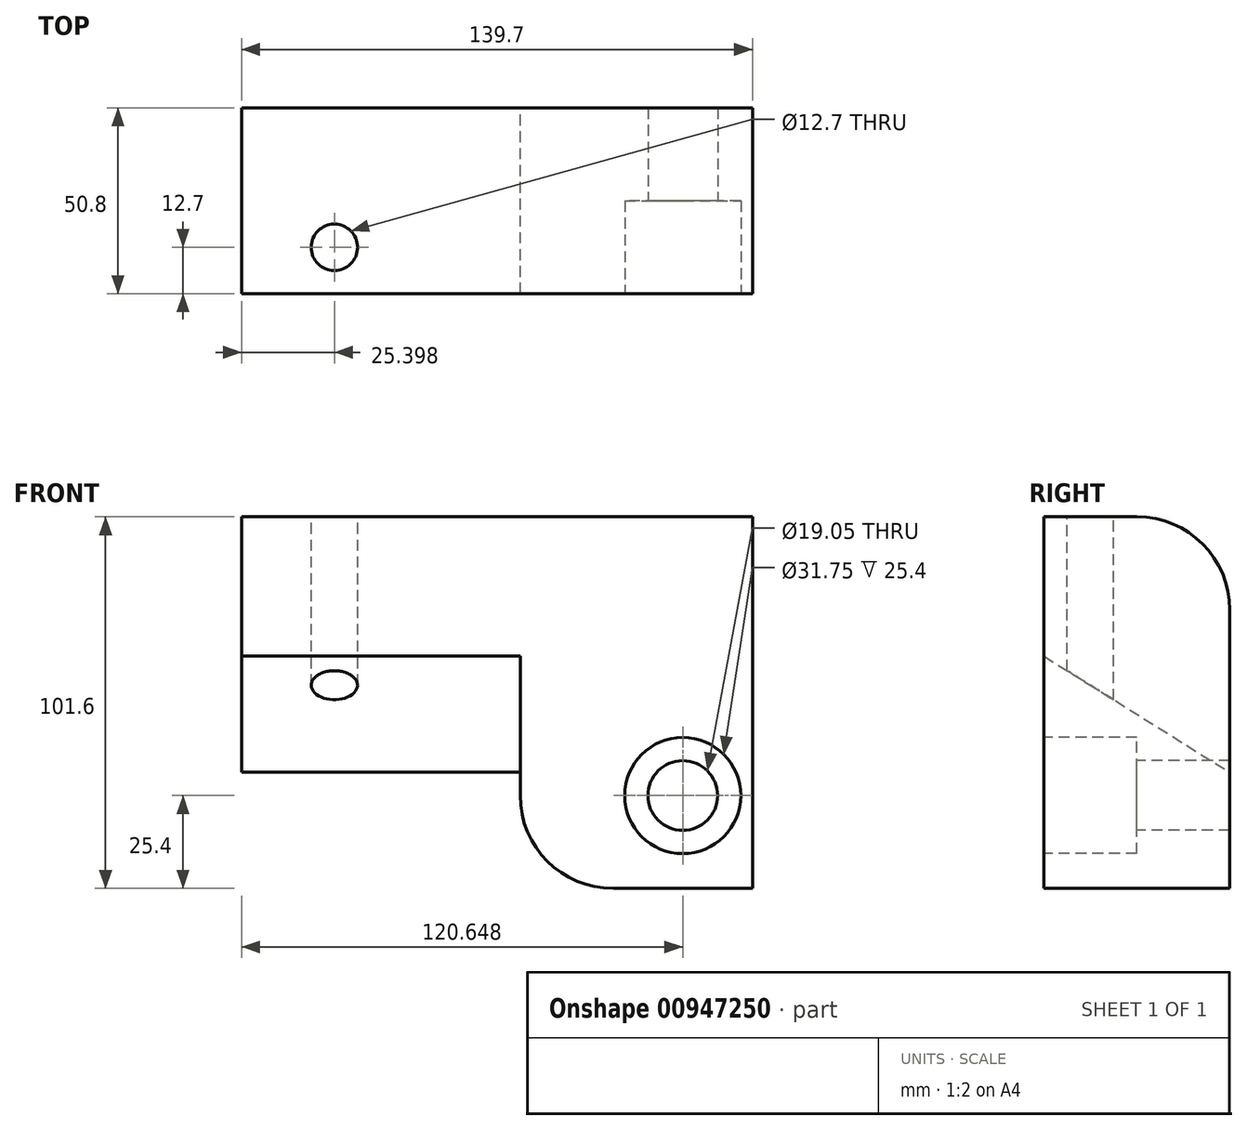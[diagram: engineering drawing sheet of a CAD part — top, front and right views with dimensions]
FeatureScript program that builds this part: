
annotation { "Feature Type Name" : "Feature", "Feature Type Description" : "" }
export const myFeature = defineFeature(function(context is Context, id is Id, definition is map)
    precondition{}
    {
        {
            var Q0;
            Q0=qCreatedBy(makeId("Front.planeOp"),FACE);
            var sketch = newSketch(context, id + "F0", { "sketchPlane" : qUnion([Q0])});
            skLineSegment(sketch, "E0.bottom", {"start": v(2.18, 50.8) * mm, "end": v(65.68, 50.8) * mm});
            skLineSegment(sketch, "E0.top", {"start": v(2.18, -50.8) * mm, "end": v(65.68, -50.8) * mm});
            skLineSegment(sketch, "E0.left", {"start": v(2.18, 50.8) * mm, "end": v(2.18, -50.8) * mm});
            skLineSegment(sketch, "E0.right", {"start": v(65.68, 50.8) * mm, "end": v(65.68, -50.8) * mm});
            skPoint(sketch, "E0.middle", {"position": v(33.93, 0) * mm});
            skLineSegment(sketch, "E1.bottom", {"start": v(2.18, 50.8) * mm, "end": v(-74.02, 50.8) * mm});
            skLineSegment(sketch, "E1.top", {"start": v(2.18, -19.05) * mm, "end": v(-74.02, -19.05) * mm});
            skLineSegment(sketch, "E1.left", {"start": v(2.18, 50.8) * mm, "end": v(2.18, -19.05) * mm});
            skLineSegment(sketch, "E1.right", {"start": v(-74.02, 50.8) * mm, "end": v(-74.02, -19.05) * mm});
            skCircle(sketch, "E2", {"center": v(46.63, -25.4) * mm, "radius": 15.88 * mm});
            skSolve(sketch);
        }
        {
            var Q0;
            Q0=makeQuery(id+"F0.imprint","IMPRINT",FACE,{"disambiguationData":[TD([[makeQuery(id+"F0.imprint","IMPRINT",EDGE,{"derivedFrom":sQuery(id+"F0.wireOp",EDGE,"E0.bottom")}),-1.0]])]});
            var Q1;
            Q1=makeQuery(id+"F0.imprint","IMPRINT",FACE,{"disambiguationData":[TD([[makeQuery(id+"F0.imprint","IMPRINT",EDGE,{"derivedFrom":sQuery(id+"F0.wireOp",EDGE,"E2")}),1.0]])]});
            var Q2;
            Q2=makeQuery(id+"F0.imprint","IMPRINT",FACE,{"disambiguationData":[TD([[makeQuery(id+"F0.imprint","IMPRINT",EDGE,{"derivedFrom":sQuery(id+"F0.wireOp",EDGE,"E1.bottom")}),1.0]])]});
            extrude(context, id + "F1", {"entities" : qUnion([Q0, Q1, Q2]), "depth" : 50.8 * mm, "offsetDistance" : 25.4 * mm});
        }
        {
            var Q0;
            Q0=makeQuery(id+"F1.opExtrude","SWEPT_EDGE",EDGE,{"disambiguationData":[OSD([sQuery(id+"F0.wireOp",EDGE,"E0.top"),sQuery(id+"F0.wireOp",EDGE,"E0.left")])]});
            fillet(context, id + "F2", {"entities" : qUnion([Q0]), "radius" : 25.4 * mm, "tangentPropagation" : true, "allowEdgeOverflow" : false});
        }
        {
            var Q0;
            Q0=makeQuery(id+"F1.opExtrude","CAP_EDGE",EDGE,{"disambiguationData":[OSD([sQuery(id+"F0.wireOp",EDGE,"E0.bottom"),sQuery(id+"F0.wireOp",EDGE,"E1.bottom")])],"isStart":true});
            fillet(context, id + "F3", {"entities" : qUnion([Q0]), "radius" : 25.4 * mm, "tangentPropagation" : true, "allowEdgeOverflow" : false});
        }
        {
            var Q0;
            Q0=makeQuery(id+"F1.opExtrude","SWEPT_FACE",FACE,{"disambiguationData":[OSD([sQuery(id+"F0.wireOp",EDGE,"E0.bottom"),sQuery(id+"F0.wireOp",EDGE,"E1.bottom")])]});
            var sketch = newSketch(context, id + "F4", { "sketchPlane" : qUnion([Q0])});
            skCircle(sketch, "E3", {"center": v(-48.62, -38.1) * mm, "radius": 6.35 * mm});
            skLineSegment(sketch, "E4.bottom", {"start": v(-74.02, -25.4) * mm, "end": v(-4.17, -25.4) * mm});
            skLineSegment(sketch, "E4.top", {"start": v(-74.02, -50.8) * mm, "end": v(-4.17, -50.8) * mm});
            skLineSegment(sketch, "E4.left", {"start": v(-74.02, -25.4) * mm, "end": v(-74.02, -50.8) * mm});
            skLineSegment(sketch, "E4.right", {"start": v(-4.17, -25.4) * mm, "end": v(-4.17, -50.8) * mm});
            skSolve(sketch);
        }
        {
            var Q0;
            Q0=makeQuery(id+"F1.opExtrude","CAP_EDGE",EDGE,{"disambiguationData":[OSD([sQuery(id+"F0.wireOp",EDGE,"E1.top")])],"isStart":false});
            chamfer(context, id + "F5", {"entities" : qUnion([Q0]), "chamferType" : ChamferType.OFFSET_ANGLE, "width" : 50.8 * mm, "oppositeDirection" : false, "angle" : 32 * degree, "tangentPropagation" : true});
        }
        {
            var Q0;
            Q0=makeQuery(id+"F1.opExtrude","CAP_FACE",FACE,{"disambiguationData":[OSD([sQuery(id+"F0.wireOp",EDGE,"E0.bottom"),sQuery(id+"F0.wireOp",EDGE,"E0.top"),sQuery(id+"F0.wireOp",EDGE,"E0.left"),sQuery(id+"F0.wireOp",EDGE,"E0.right"),sQuery(id+"F0.wireOp",EDGE,"E1.bottom"),sQuery(id+"F0.wireOp",EDGE,"E1.top"),sQuery(id+"F0.wireOp",EDGE,"E1.right")])],"isStart":false});
            var sketch = newSketch(context, id + "F6", { "sketchPlane" : qUnion([Q0])});
            skLineSegment(sketch, "E5.bottom", {"start": v(65.68, -50.8) * mm, "end": v(2.18, -50.8) * mm});
            skLineSegment(sketch, "E5.top", {"start": v(65.68, 5.67) * mm, "end": v(2.18, 5.67) * mm});
            skLineSegment(sketch, "E5.left", {"start": v(65.68, -50.8) * mm, "end": v(65.68, 5.67) * mm});
            skLineSegment(sketch, "E5.right", {"start": v(2.18, -50.8) * mm, "end": v(2.18, 5.67) * mm});
            skPoint(sketch, "E6", {"position": v(46.63, -25.4) * mm});
            skSolve(sketch);
        }
        {
            var Q0;
            Q0=sQuery(id+"F4.wireOp",VERTEX,"E3.center");
            var Q1;
            Q1=makeQuery(id+"F1.opExtrude","SWEPT_BODY",BODY,{"disambiguationData":[OSD([sQuery(id+"F0.wireOp",EDGE,"E0.bottom"),sQuery(id+"F0.wireOp",EDGE,"E0.top"),sQuery(id+"F0.wireOp",EDGE,"E0.left"),sQuery(id+"F0.wireOp",EDGE,"E0.right"),sQuery(id+"F0.wireOp",EDGE,"E1.bottom"),sQuery(id+"F0.wireOp",EDGE,"E1.top"),sQuery(id+"F0.wireOp",EDGE,"E1.right")])]});
            hole(context, id + "F7", {"style" : HoleStyle.SIMPLE, "endStyle" : HoleEndStyle.THROUGH, "holeDiameter" : 12.7 * mm, "majorDiameter" : 6.35 * mm, "isTappedThrough" : true, "tappedDepth" : 12.7 * mm, "tapClearance" : 3, "locations" : qUnion([Q0]), "scope" : qUnion([Q1])});
        }
        {
            var Q0;
            Q0=sQuery(id+"F6.wireOp",VERTEX,"E6");
            var Q1;
            Q1=makeQuery(id+"F1.opExtrude","SWEPT_BODY",BODY,{"disambiguationData":[OSD([sQuery(id+"F0.wireOp",EDGE,"E0.bottom"),sQuery(id+"F0.wireOp",EDGE,"E0.top"),sQuery(id+"F0.wireOp",EDGE,"E0.left"),sQuery(id+"F0.wireOp",EDGE,"E0.right"),sQuery(id+"F0.wireOp",EDGE,"E1.bottom"),sQuery(id+"F0.wireOp",EDGE,"E1.top"),sQuery(id+"F0.wireOp",EDGE,"E1.right")])]});
            hole(context, id + "F8", {"style" : HoleStyle.C_BORE, "endStyle" : HoleEndStyle.THROUGH, "holeDiameter" : 19.05 * mm, "cBoreDiameter" : 31.75 * mm, "cBoreDepth" : 25.4 * mm, "majorDiameter" : 6.35 * mm, "isTappedThrough" : true, "tappedDepth" : 12.7 * mm, "tapClearance" : 3, "locations" : qUnion([Q0]), "scope" : qUnion([Q1])});
        }
    });
